# Revit family: Storage-Teknion-CAMD_Mini_Drawer_Undermount_Add_On-2021
name_source: partatom
category: Furniture
units: mm (PartAtom-declared; Revit-internal decimal feet)

## family parameters
Always vertical = Yes
Cut with Voids When Loaded = No
OmniClass Number = 23.40.20.00
OmniClass Title = General Furniture and Specialties
Room Calculation Point = No
Shared = Yes
Work Plane-Based = No

## types (2) — shared parameters
Assembly Code = E2020200
Manufacturer = Teknion
Manufacturer Fax = 416.661.4586
Part Number = CAMD
Product Documentation Link = https://www.teknion.com
Product Line = Chronicle
Product Page URL = https://www.teknion.com
Series = Chronicle
Sustainability Data = https://www.teknion.com
URL = www.teknion.com
Unit Weight URL = http://www.teknion.com
Warranty = http://www.teknion.com
zero-valued in all types: Default Elevation

## per-type parameters (varying)
| type | Cork Divider Insert | Description | Model | Standard Mni Drawer |
| Standard Mini Drawer | No | Mini Drawer, Undermount Add-On, Standard Configuration | CAMDS | Yes |
| Cork Divider Insert Mini Drawer | Yes | Mini Drawer, Undermount Add-On, Cork Divider Insert Configuration | CAMDC | No |

## geometry (parser evidence)
native form markers: Sweep x3
no freeform markers — native parametric forms only
